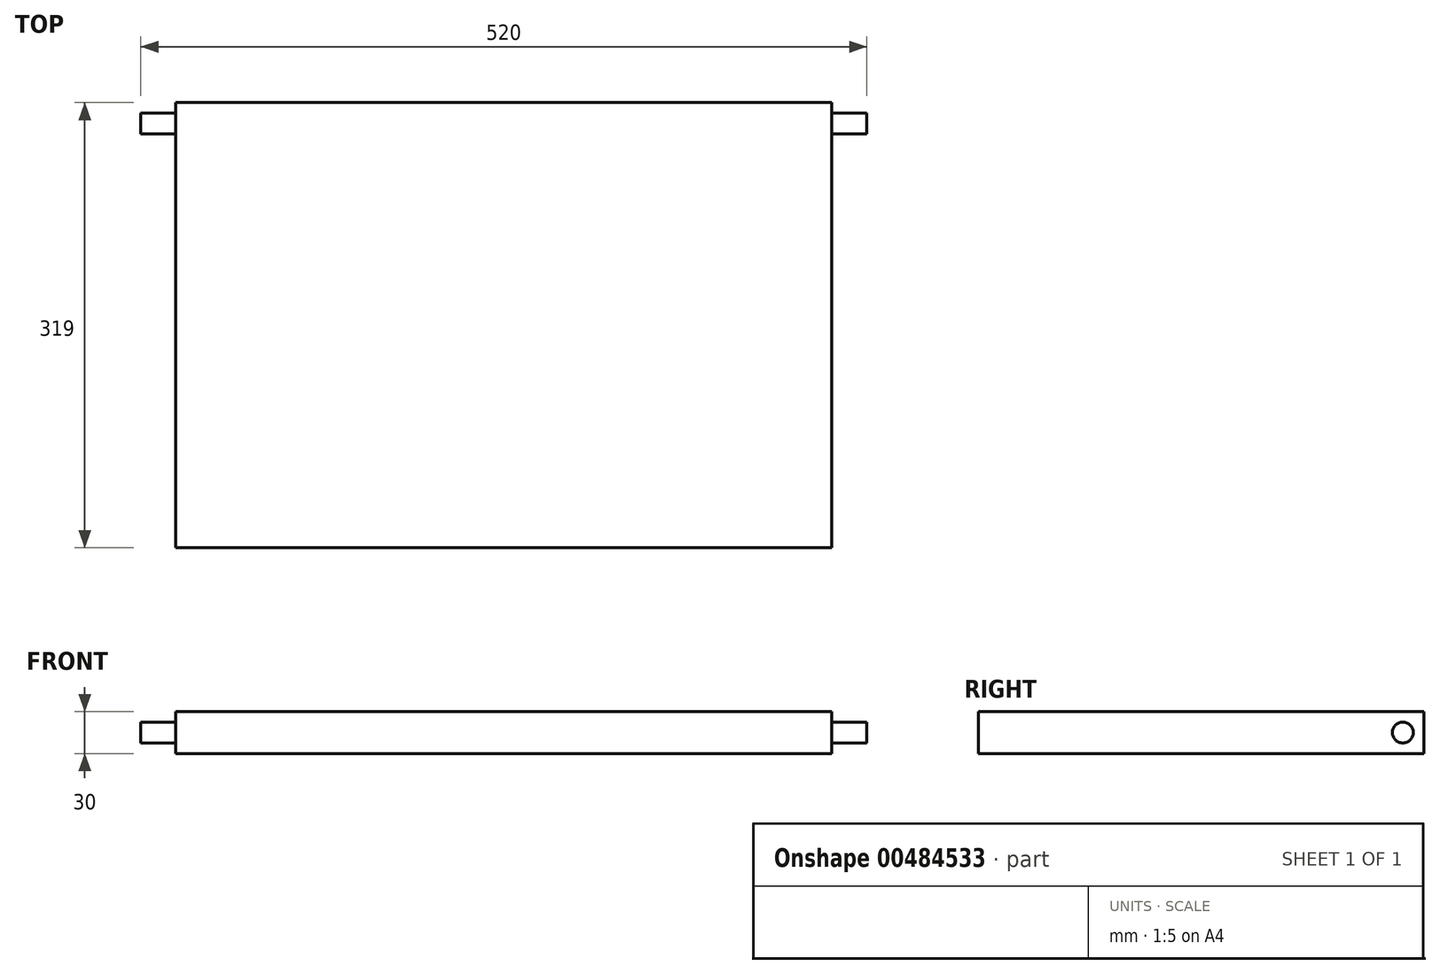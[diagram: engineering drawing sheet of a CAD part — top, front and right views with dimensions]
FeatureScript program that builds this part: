
annotation { "Feature Type Name" : "Feature", "Feature Type Description" : "" }
export const myFeature = defineFeature(function(context is Context, id is Id, definition is map)
    precondition{}
    {
        {
            var Q0;
            Q0=qCreatedBy(makeId("Top.planeOp"),FACE);
            var sketch = newSketch(context, id + "F0", { "sketchPlane" : qUnion([Q0])});
            skLineSegment(sketch, "E0.bottom", {"start": v(-509.87, -280.53) * mm, "end": v(-39.87, -280.53) * mm});
            skLineSegment(sketch, "E0.top", {"start": v(-509.87, 38.47) * mm, "end": v(-39.87, 38.47) * mm});
            skLineSegment(sketch, "E0.left", {"start": v(-509.87, -280.53) * mm, "end": v(-509.87, 38.47) * mm});
            skLineSegment(sketch, "E0.right", {"start": v(-39.87, -280.53) * mm, "end": v(-39.87, 38.47) * mm});
            skSolve(sketch);
        }
        {
            var Q0;
            Q0=qSketchRegion(id+"F0",true);
            extrude(context, id + "F1", {"entities" : qUnion([Q0]), "depth" : 30 * mm});
        }
        {
            var Q0;
            Q0=makeQuery(id+"F1.opExtrude","SWEPT_FACE",FACE,{"disambiguationData":[OSD([sQuery(id+"F0.wireOp",EDGE,"E0.left")])]});
            var sketch = newSketch(context, id + "F2", { "sketchPlane" : qUnion([Q0])});
            skCircle(sketch, "E1", {"center": v(-23.47, 15) * mm, "radius": 7.5 * mm});
            skSolve(sketch);
        }
        {
            var Q0;
            Q0=makeQuery(id+"F2.imprint","IMPRINT",FACE,{"disambiguationData":[TD([[makeQuery(id+"F2.imprint","IMPRINT",EDGE,{"derivedFrom":sQuery(id+"F2.wireOp",EDGE,"E1")}),-1.0]])]});
            extrude(context, id + "F3", {"entities" : qUnion([Q0]), "operationType" : NewBodyOperationType.ADD, "oppositeDirection" : true, "depth" : 30 * mm});
        }
        {
            var Q0;
            Q0=makeQuery(id+"F2.imprint","IMPRINT",FACE,{"disambiguationData":[TD([[makeQuery(id+"F2.imprint","IMPRINT",EDGE,{"derivedFrom":sQuery(id+"F2.wireOp",EDGE,"E1")}),1.0]])]});
            var Q1;
            Q1=qSketchRegion(id+"F2",true);
            var Q2;
            Q2=sQuery(id+"F2.wireOp",EDGE,"E1");
            extrude(context, id + "F4", {"entities" : qUnion([Q0]), "operationType" : NewBodyOperationType.ADD, "surfaceEntities" : qUnion([Q1, Q2]), "depth" : 25 * mm});
        }
        {
            var Q0;
            Q0=makeQuery(id+"F1.opExtrude","SWEPT_FACE",FACE,{"disambiguationData":[OSD([sQuery(id+"F0.wireOp",EDGE,"E0.right")])]});
            var sketch = newSketch(context, id + "F5", { "sketchPlane" : qUnion([Q0])});
            skCircle(sketch, "E2", {"center": v(23.47, 15) * mm, "radius": 7.5 * mm});
            skSolve(sketch);
        }
        {
            var Q0;
            Q0=qSketchRegion(id+"F5",true);
            extrude(context, id + "F6", {"entities" : qUnion([Q0]), "operationType" : NewBodyOperationType.ADD, "depth" : 25 * mm});
        }
    });
